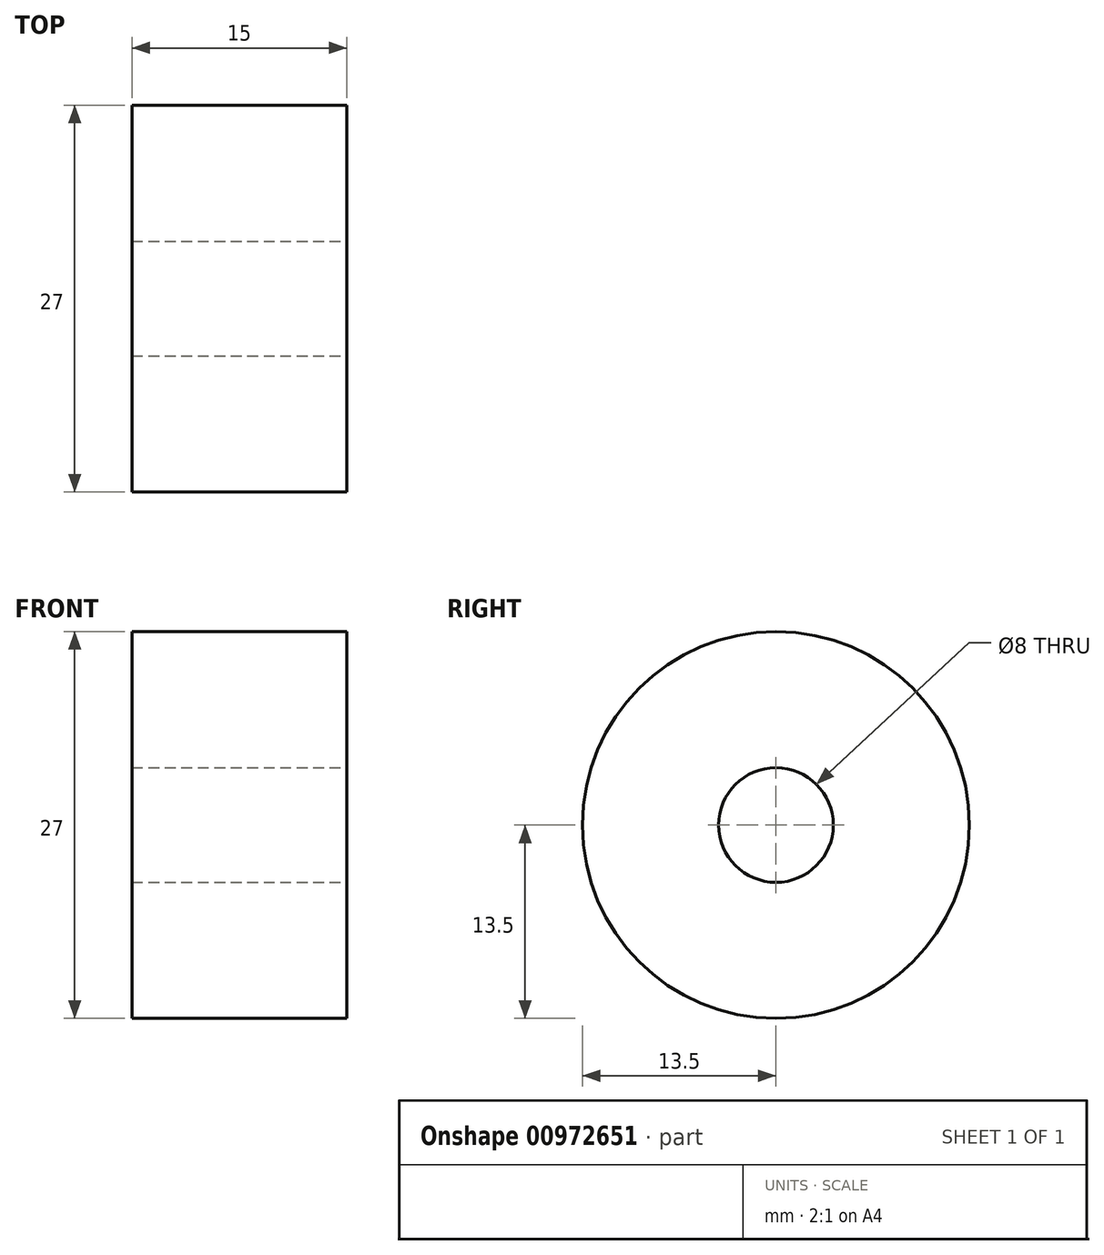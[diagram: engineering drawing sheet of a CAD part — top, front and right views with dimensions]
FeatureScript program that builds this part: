
annotation { "Feature Type Name" : "Feature", "Feature Type Description" : "" }
export const myFeature = defineFeature(function(context is Context, id is Id, definition is map)
    precondition{}
    {
        {
            var Q0;
            Q0=qCreatedBy(makeId("Front.planeOp"),FACE);
            var sketch = newSketch(context, id + "F0", { "sketchPlane" : qUnion([Q0])});
            skLineSegment(sketch, "E0", {"start": v(-7.5, 0) * mm, "end": v(7.5, 0) * mm, "construction": true});
            skLineSegment(sketch, "E1", {"start": v(-7.5, 13.5) * mm, "end": v(7.5, 13.5) * mm});
            skLineSegment(sketch, "E2", {"start": v(-7.5, 0) * mm, "end": v(-7.5, 13.5) * mm});
            skLineSegment(sketch, "E3", {"start": v(7.5, 13.5) * mm, "end": v(7.5, 0) * mm});
            skLineSegment(sketch, "E4", {"start": v(-7.5, 0) * mm, "end": v(7.5, 0) * mm});
            skSolve(sketch);
        }
        {
            var Q0;
            Q0=makeQuery(id+"F0.imprint","IMPRINT",FACE,{"disambiguationData":[TD([[makeQuery(id+"F0.imprint","IMPRINT",EDGE,{"derivedFrom":sQuery(id+"F0.wireOp",EDGE,"E1")}),-1.0]])]});
            var Q1;
            Q1=sQuery(id+"F0.wireOp",EDGE,"E4");
            revolve(context, id + "F1", {"surfaceOperationType" : NewSurfaceOperationType.NEW, "entities" : qUnion([Q0]), "axis" : qUnion([Q1]), "revolveType" : RevolveType.FULL, "oppositeDirection" : true});
        }
        {
            var Q0;
            Q0=makeQuery(id+"F1.opRevolve","SWEPT_FACE",FACE,{"disambiguationData":[OSD([sQuery(id+"F0.wireOp",EDGE,"E3")])]});
            var sketch = newSketch(context, id + "F2", { "sketchPlane" : qUnion([Q0])});
            skCircle(sketch, "E5", {"center": v(0, 0) * mm, "radius": 4 * mm});
            skSolve(sketch);
        }
        {
            var Q0;
            Q0=makeQuery(id+"F2.imprint","IMPRINT",FACE,{"disambiguationData":[TD([[makeQuery(id+"F2.imprint","IMPRINT",EDGE,{"derivedFrom":sQuery(id+"F2.wireOp",EDGE,"E5")}),1.0]])]});
            extrude(context, id + "F3", {"entities" : qUnion([Q0]), "operationType" : NewBodyOperationType.REMOVE, "endBound" : BoundingType.THROUGH_ALL, "oppositeDirection" : true, "depth" : 25 * mm, "offsetDistance" : 25 * mm});
        }
    });
